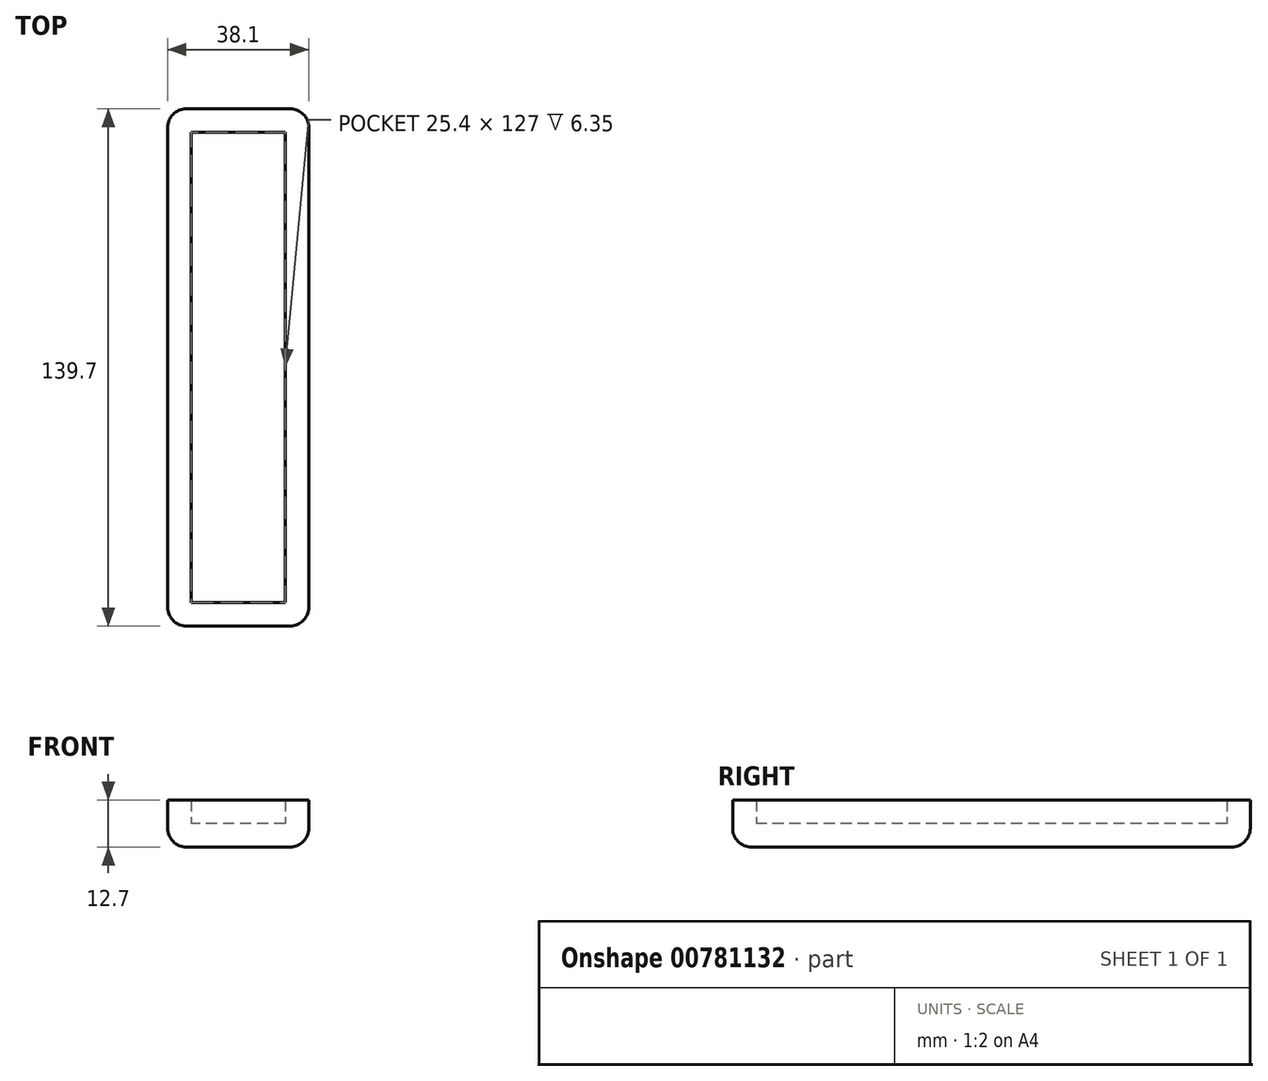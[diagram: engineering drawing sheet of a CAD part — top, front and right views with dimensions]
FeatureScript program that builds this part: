
annotation { "Feature Type Name" : "Feature", "Feature Type Description" : "" }
export const myFeature = defineFeature(function(context is Context, id is Id, definition is map)
    precondition{}
    {
        {
            var Q0;
            Q0=qCreatedBy(makeId("Top.planeOp"),FACE);
            var sketch = newSketch(context, id + "F0", { "sketchPlane" : qUnion([Q0])});
            skLineSegment(sketch, "E0.bottom", {"start": v(12.7, 63.5) * mm, "end": v(-12.7, 63.5) * mm});
            skLineSegment(sketch, "E0.top", {"start": v(12.7, -63.5) * mm, "end": v(-12.7, -63.5) * mm});
            skLineSegment(sketch, "E0.left", {"start": v(12.7, 63.5) * mm, "end": v(12.7, -63.5) * mm});
            skLineSegment(sketch, "E0.right", {"start": v(-12.7, 63.5) * mm, "end": v(-12.7, -63.5) * mm});
            skPoint(sketch, "E0.middle", {"position": v(0, 0) * mm});
            skLineSegment(sketch, "E1.bottom", {"start": v(19.05, 69.85) * mm, "end": v(-19.05, 69.85) * mm});
            skLineSegment(sketch, "E1.top", {"start": v(19.05, -69.85) * mm, "end": v(-19.05, -69.85) * mm});
            skLineSegment(sketch, "E1.left", {"start": v(19.05, 69.85) * mm, "end": v(19.05, -69.85) * mm});
            skLineSegment(sketch, "E1.right", {"start": v(-19.05, 69.85) * mm, "end": v(-19.05, -69.85) * mm});
            skSolve(sketch);
        }
        {
            var Q0;
            Q0=makeQuery(id+"F0.imprint","IMPRINT",FACE,{"disambiguationData":[TD([[makeQuery(id+"F0.imprint","IMPRINT",EDGE,{"derivedFrom":sQuery(id+"F0.wireOp",EDGE,"E0.bottom")}),-1.0]])]});
            extrude(context, id + "F1", {"entities" : qUnion([Q0]), "depth" : 12.7 * mm, "offsetDistance" : 25.4 * mm});
        }
        {
            var Q0;
            Q0=makeQuery(id+"F0.imprint","IMPRINT",FACE,{"disambiguationData":[TD([[makeQuery(id+"F0.imprint","IMPRINT",EDGE,{"derivedFrom":sQuery(id+"F0.wireOp",EDGE,"E0.bottom")}),1.0]])]});
            extrude(context, id + "F2", {"entities" : qUnion([Q0]), "operationType" : NewBodyOperationType.ADD, "depth" : 6.35 * mm, "offsetDistance" : 25.4 * mm});
        }
        {
            var Q0;
            Q0=makeQuery(id+"F1.opExtrude","SWEPT_EDGE",EDGE,{"disambiguationData":[OSD([sQuery(id+"F0.wireOp",EDGE,"E1.top"),sQuery(id+"F0.wireOp",EDGE,"E1.right")])]});
            var Q1;
            Q1=makeQuery(id+"F1.opExtrude","SWEPT_EDGE",EDGE,{"disambiguationData":[OSD([sQuery(id+"F0.wireOp",EDGE,"E1.top"),sQuery(id+"F0.wireOp",EDGE,"E1.left")])]});
            var Q2;
            Q2=makeQuery(id+"F1.opExtrude","SWEPT_EDGE",EDGE,{"disambiguationData":[OSD([sQuery(id+"F0.wireOp",EDGE,"E1.bottom"),sQuery(id+"F0.wireOp",EDGE,"E1.left")])]});
            var Q3;
            Q3=makeQuery(id+"F1.opExtrude","SWEPT_EDGE",EDGE,{"disambiguationData":[OSD([sQuery(id+"F0.wireOp",EDGE,"E1.bottom"),sQuery(id+"F0.wireOp",EDGE,"E1.right")])]});
            var Q4;
            Q4=makeQuery(id+"F1.opExtrude","CAP_EDGE",EDGE,{"disambiguationData":[OSD([sQuery(id+"F0.wireOp",EDGE,"E1.bottom")])],"isStart":true});
            var Q5;
            Q5=makeQuery(id+"F1.opExtrude","CAP_EDGE",EDGE,{"disambiguationData":[OSD([sQuery(id+"F0.wireOp",EDGE,"E1.right")])],"isStart":true});
            fillet(context, id + "F3", {"entities" : qUnion([Q0, Q1, Q2, Q3, Q4, Q5]), "radius" : 5.08 * mm, "tangentPropagation" : true, "allowEdgeOverflow" : false});
        }
        {
            var Q0;
            Q0=makeQuery(id+"F1.opExtrude","CAP_EDGE",EDGE,{"disambiguationData":[OSD([sQuery(id+"F0.wireOp",EDGE,"E1.left")])],"isStart":true});
            fillet(context, id + "F4", {"entities" : qUnion([Q0]), "radius" : 5.08 * mm, "tangentPropagation" : true, "allowEdgeOverflow" : false});
        }
    });
